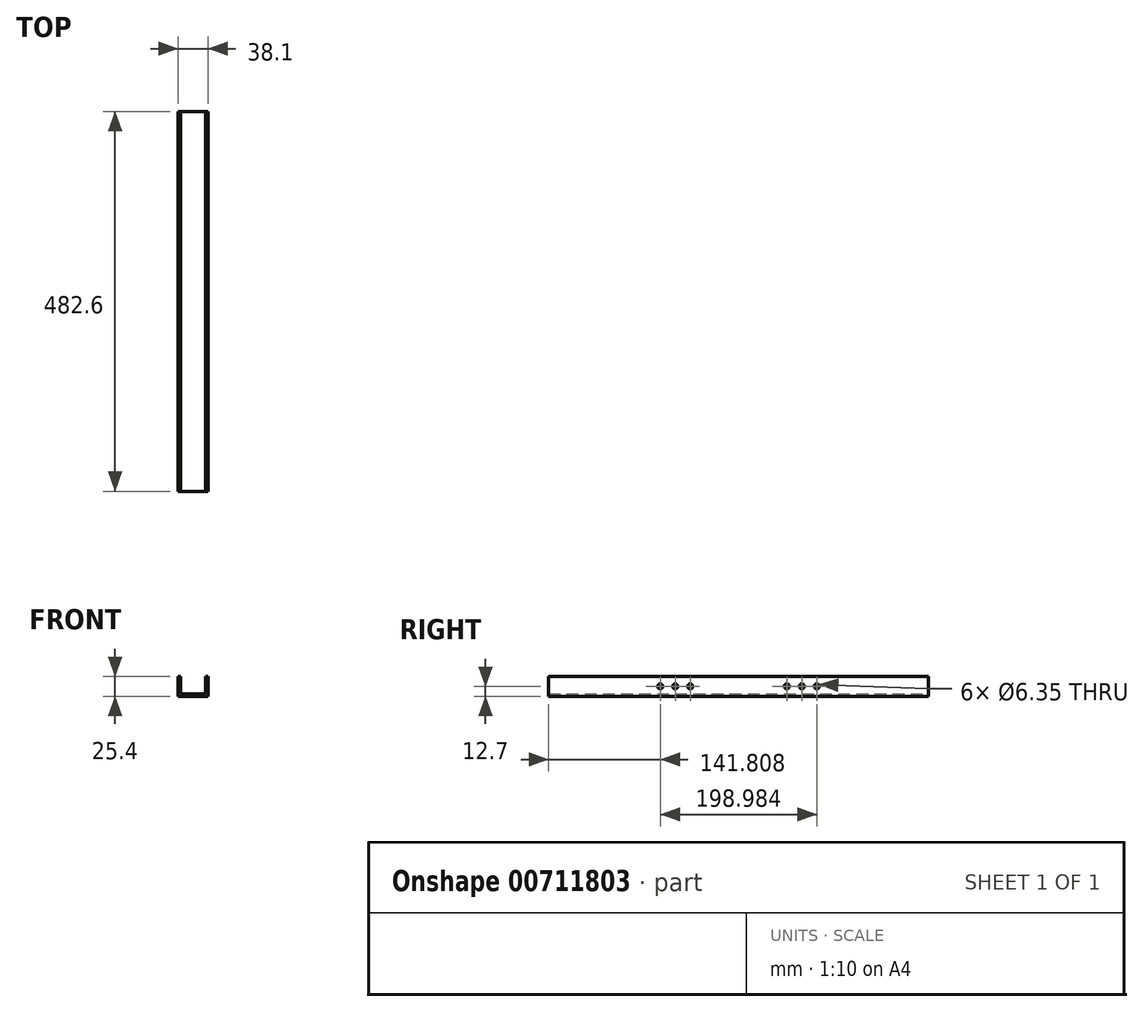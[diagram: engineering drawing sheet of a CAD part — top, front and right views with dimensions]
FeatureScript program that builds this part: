
annotation { "Feature Type Name" : "Feature", "Feature Type Description" : "" }
export const myFeature = defineFeature(function(context is Context, id is Id, definition is map)
    precondition{}
    {
        {
            var Q0;
            Q0=qCreatedBy(makeId("Front.planeOp"),FACE);
            var sketch = newSketch(context, id + "F0", { "sketchPlane" : qUnion([Q0])});
            skLineSegment(sketch, "E0.bottom", {"start": v(0, 0) * mm, "end": v(38.1, 0) * mm});
            skLineSegment(sketch, "E0.top", {"start": v(0, 25.4) * mm, "end": v(3.18, 25.4) * mm});
            skLineSegment(sketch, "E0.left", {"start": v(0, 0) * mm, "end": v(0, 25.4) * mm});
            skLineSegment(sketch, "E0.right", {"start": v(38.1, 0) * mm, "end": v(38.1, 25.4) * mm});
            skLineSegment(sketch, "E1", {"start": v(3.18, 3.17) * mm, "end": v(3.18, 25.4) * mm});
            skLineSegment(sketch, "E2", {"start": v(34.92, 25.4) * mm, "end": v(34.92, 3.18) * mm});
            skLineSegment(sketch, "E3", {"start": v(34.92, 3.18) * mm, "end": v(3.18, 3.17) * mm});
            skLineSegment(sketch, "E4.trimOffspring", {"start": v(34.92, 25.4) * mm, "end": v(38.1, 25.4) * mm});
            skSolve(sketch);
        }
        {
            var Q0;
            Q0 = qSketchRegion(id + "F0", true);
            extrude(context, id + "F1", {"entities" : qUnion([Q0]), "depth" : 482.6 * mm, "offsetDistance" : 25.4 * mm});
        }
        {
            var Q0;
            Q0=makeQuery(id+"F1.opExtrude","SWEPT_FACE",FACE,{"disambiguationData":[OSD([sQuery(id+"F0.wireOp",EDGE,"E0.right")])]});
            var sketch = newSketch(context, id + "F2", { "sketchPlane" : qUnion([Q0])});
            skCircle(sketch, "E5", {"center": v(-141.8, 12.7) * mm, "radius": 3.18 * mm});
            skCircle(sketch, "E6", {"center": v(-160.86, 12.7) * mm, "radius": 3.18 * mm});
            skCircle(sketch, "E7", {"center": v(-179.9, 12.7) * mm, "radius": 3.18 * mm});
            skCircle(sketch, "E8", {"center": v(-302.7, 12.7) * mm, "radius": 3.18 * mm});
            skCircle(sketch, "E9", {"center": v(-321.74, 12.7) * mm, "radius": 3.18 * mm});
            skCircle(sketch, "E10", {"center": v(-340.8, 12.7) * mm, "radius": 3.18 * mm});
            skSolve(sketch);
        }
        {
            var Q0;
            Q0 = qSketchRegion(id + "F2", true);
            extrude(context, id + "F3", {"entities" : qUnion([Q0]), "operationType" : NewBodyOperationType.REMOVE, "oppositeDirection" : true, "depth" : 6.35 * mm, "offsetDistance" : 25.4 * mm});
        }
    });
